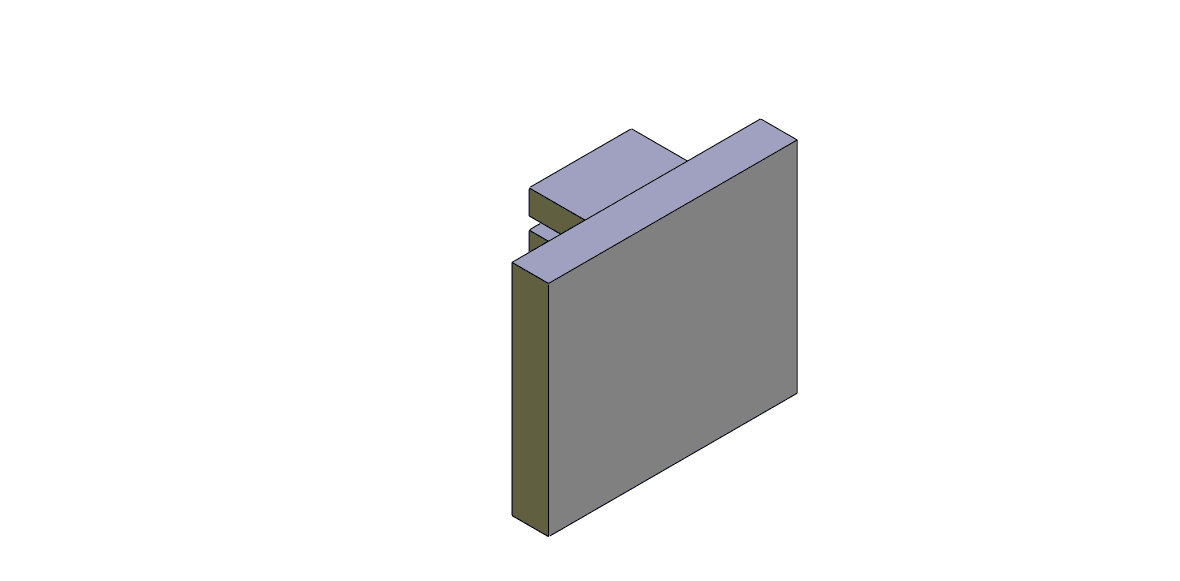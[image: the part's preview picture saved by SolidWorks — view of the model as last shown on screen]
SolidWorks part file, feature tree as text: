
SOLIDWORKS PART (.sldprt)
format: sldprt  version: not decoded by parser v0  size: 273,408 bytes
history: native  units: mm
features: sketch x6, extrude x4, plane x3, material x1, cut_extrude x1 (+9 scaffold rows collapsed)
feature tree (24):
  scaffold x9  (default folders/planes/origin — collapsed)
  material  "Material <not specified>"
  plane  "Plan de face"
  plane  "Plan de dessus"
  plane  "Plan de droite"
  sketch  "Sketch1"  dims[c1.D1=55.0mm c1.D2=~70.180276mm c2.D1=43.0mm c2.D2=10.0mm c2.D3=10.0mm c2.D4=15.0mm c2.D5=35.0mm c2.D6=10.0mm c2.D7=5.0mm c2.D8=90.0mm c3.D1=10.0mm c3.D2=10.0mm c3.D3=43.0mm c3.D4=10.0mm c3.D5=10.0mm c3.D6=10.0mm c3.D7=45.0mm c3.D8=45.0mm]
  extrude  "Boss-Extrude1"  Depth=42mm
  sketch  "Sketch2"  dims[D1=16.0mm D2=10.0mm D3=16.0mm]
  extrude  "Boss-Extrude2"  Depth=46mm
  sketch  "Sketch3"  dims[D1=20.0mm]
  extrude  "Boss-Extrude3"  [1 undecoded]
  sketch  "Sketch4"  dims[D1=20.0mm D2=20.0mm D3=10.0mm D4=10.0mm]
  extrude  "Boss-Extrude4"  [1 undecoded]
  sketch  "Sketch5"
  sketch  "Sketch6"  dims[D1=5.0mm D2=10.5mm D3=14.0mm]
  cut_extrude  "Cut-Extrude1"  [1 undecoded]
decode coverage: 7 of 11 modeling features carry decoded parameters
note: ~ marks probable driven/reference dimensions
note: 3 parameter values undecoded
summary: no parameter record found for 3 features
note: suppression state not decoded; provenance and decode notes live in map.json
